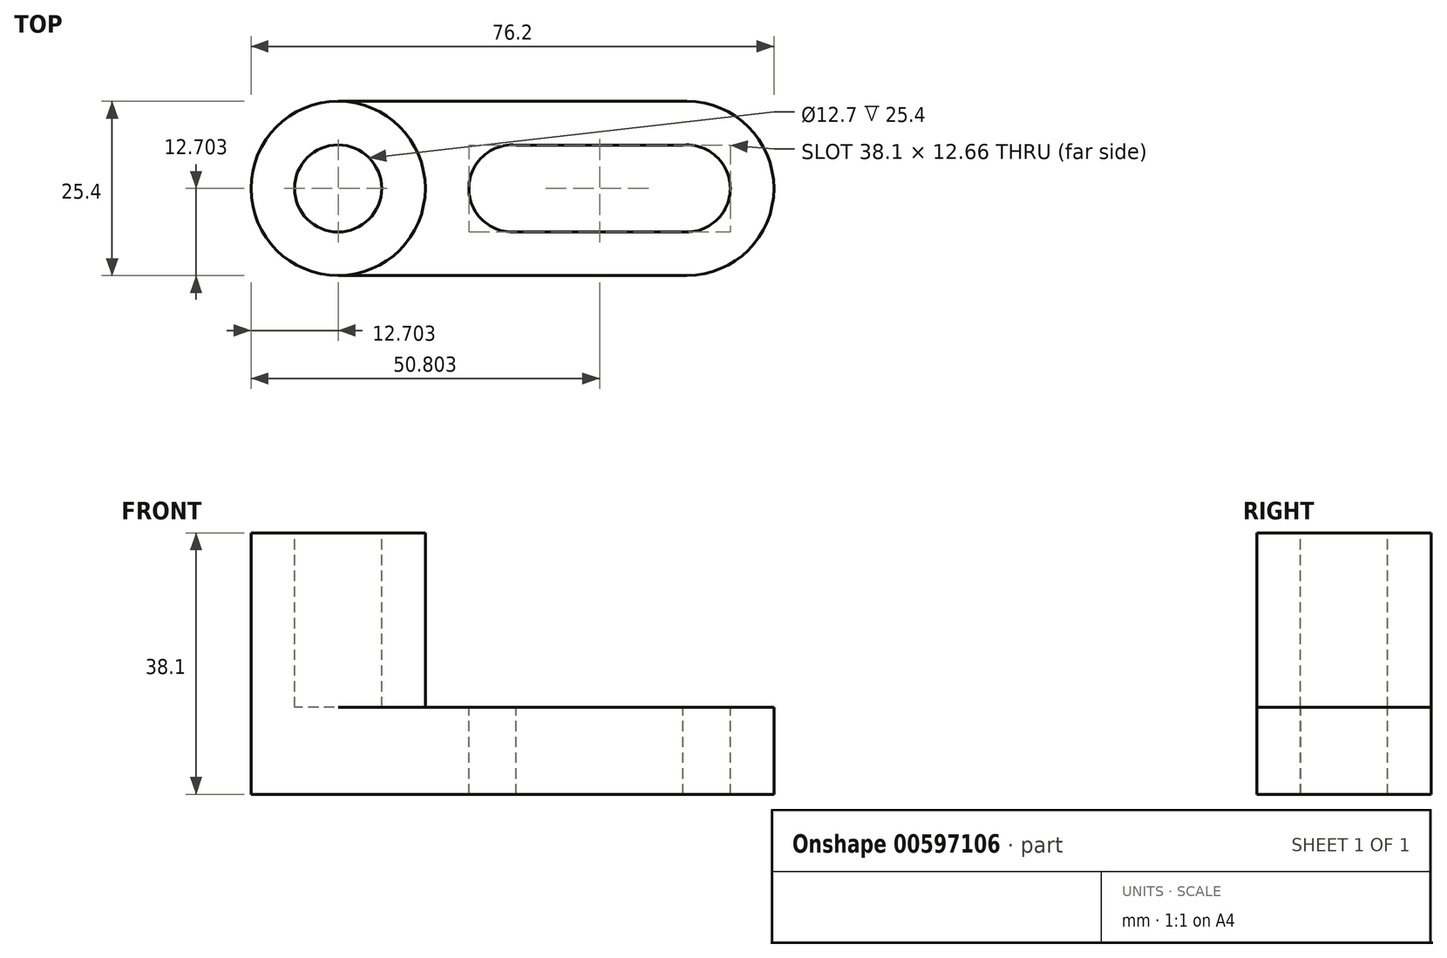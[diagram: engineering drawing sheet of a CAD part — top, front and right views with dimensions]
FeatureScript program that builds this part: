
annotation { "Feature Type Name" : "Feature", "Feature Type Description" : "" }
export const myFeature = defineFeature(function(context is Context, id is Id, definition is map)
    precondition{}
    {
        {
            var Q0;
            Q0=qCreatedBy(makeId("Top.planeOp"),FACE);
            var sketch = newSketch(context, id + "F0", { "sketchPlane" : qUnion([Q0])});
            skLineSegment(sketch, "E0", {"start": v(-44.26, 57.34) * mm, "end": v(6.54, 57.34) * mm});
            skLineSegment(sketch, "E1", {"start": v(6.54, 57.34) * mm, "end": v(6.54, 31.94) * mm});
            skLineSegment(sketch, "E2", {"start": v(6.54, 31.94) * mm, "end": v(-44.26, 31.94) * mm});
            skLineSegment(sketch, "E3", {"start": v(-44.26, 31.94) * mm, "end": v(-44.26, 57.34) * mm});
            skArc(sketch, "E4", {"start": v(-44.26, 57.34) * mm, "mid": v(-56.96, 44.64) * mm, "end": v(-44.26, 31.94) * mm});
            skArc(sketch, "E5", {"start": v(6.54, 31.94) * mm, "mid": v(19.24, 44.64) * mm, "end": v(6.54, 57.34) * mm});
            skSolve(sketch);
        }
        {
            var Q0;
            Q0 = qSketchRegion(id + "F0", true);
            extrude(context, id + "F1", {"entities" : qUnion([Q0]), "depth" : 12.7 * mm, "offsetDistance" : 25.4 * mm});
        }
        {
            var Q0;
            Q0=makeQuery(id+"F1.opExtrude","CAP_FACE",FACE,{"disambiguationData":[OSD([sQuery(id+"F0.wireOp",EDGE,"E0"),sQuery(id+"F0.wireOp",EDGE,"E2"),sQuery(id+"F0.wireOp",EDGE,"E4"),sQuery(id+"F0.wireOp",EDGE,"E5")])],"isStart":false});
            var sketch = newSketch(context, id + "F2", { "sketchPlane" : qUnion([Q0])});
            skCircle(sketch, "E6", {"center": v(-44.26, 44.64) * mm, "radius": 12.7 * mm});
            skSolve(sketch);
        }
        {
            var Q0;
            Q0 = qSketchRegion(id + "F2", true);
            extrude(context, id + "F3", {"entities" : qUnion([Q0]), "operationType" : NewBodyOperationType.ADD, "depth" : 25.4 * mm, "offsetDistance" : 25.4 * mm});
        }
        {
            var Q0;
            Q0=makeQuery(id+"F3.opExtrude","CAP_FACE",FACE,{"disambiguationData":[OSD([sQuery(id+"F2.wireOp",EDGE,"E6")])],"isStart":false});
            var sketch = newSketch(context, id + "F4", { "sketchPlane" : qUnion([Q0])});
            skCircle(sketch, "E7", {"center": v(-44.26, 44.64) * mm, "radius": 6.35 * mm});
            skSolve(sketch);
        }
        {
            var Q0;
            Q0 = qSketchRegion(id + "F4", true);
            extrude(context, id + "F5", {"entities" : qUnion([Q0]), "operationType" : NewBodyOperationType.REMOVE, "oppositeDirection" : true, "depth" : 25.4 * mm, "offsetDistance" : 25.4 * mm});
        }
        {
            var Q0;
            Q0=makeQuery(id+"F1.opExtrude","CAP_FACE",FACE,{"disambiguationData":[OSD([sQuery(id+"F0.wireOp",EDGE,"E0"),sQuery(id+"F0.wireOp",EDGE,"E2"),sQuery(id+"F0.wireOp",EDGE,"E4"),sQuery(id+"F0.wireOp",EDGE,"E5")])],"isStart":false});
            var sketch = newSketch(context, id + "F6", { "sketchPlane" : qUnion([Q0])});
            skCircle(sketch, "E8", {"center": v(6.54, 44.64) * mm, "radius": 6.35 * mm});
            skCircle(sketch, "E9", {"center": v(-18.86, 44.64) * mm, "radius": 6.35 * mm});
            skLineSegment(sketch, "E10", {"start": v(-18.34, 50.97) * mm, "end": v(7.06, 50.97) * mm});
            skLineSegment(sketch, "E11", {"start": v(7.06, 50.97) * mm, "end": v(7.06, 38.31) * mm});
            skLineSegment(sketch, "E12", {"start": v(7.06, 38.31) * mm, "end": v(-18.34, 38.31) * mm});
            skLineSegment(sketch, "E13", {"start": v(-18.34, 38.31) * mm, "end": v(-18.34, 50.97) * mm});
            skSolve(sketch);
        }
        {
            var Q0;
            Q0 = qSketchRegion(id + "F6", true);
            extrude(context, id + "F7", {"entities" : qUnion([Q0]), "operationType" : NewBodyOperationType.REMOVE, "oppositeDirection" : true, "depth" : 12.7 * mm, "offsetDistance" : 25.4 * mm});
        }
    });
